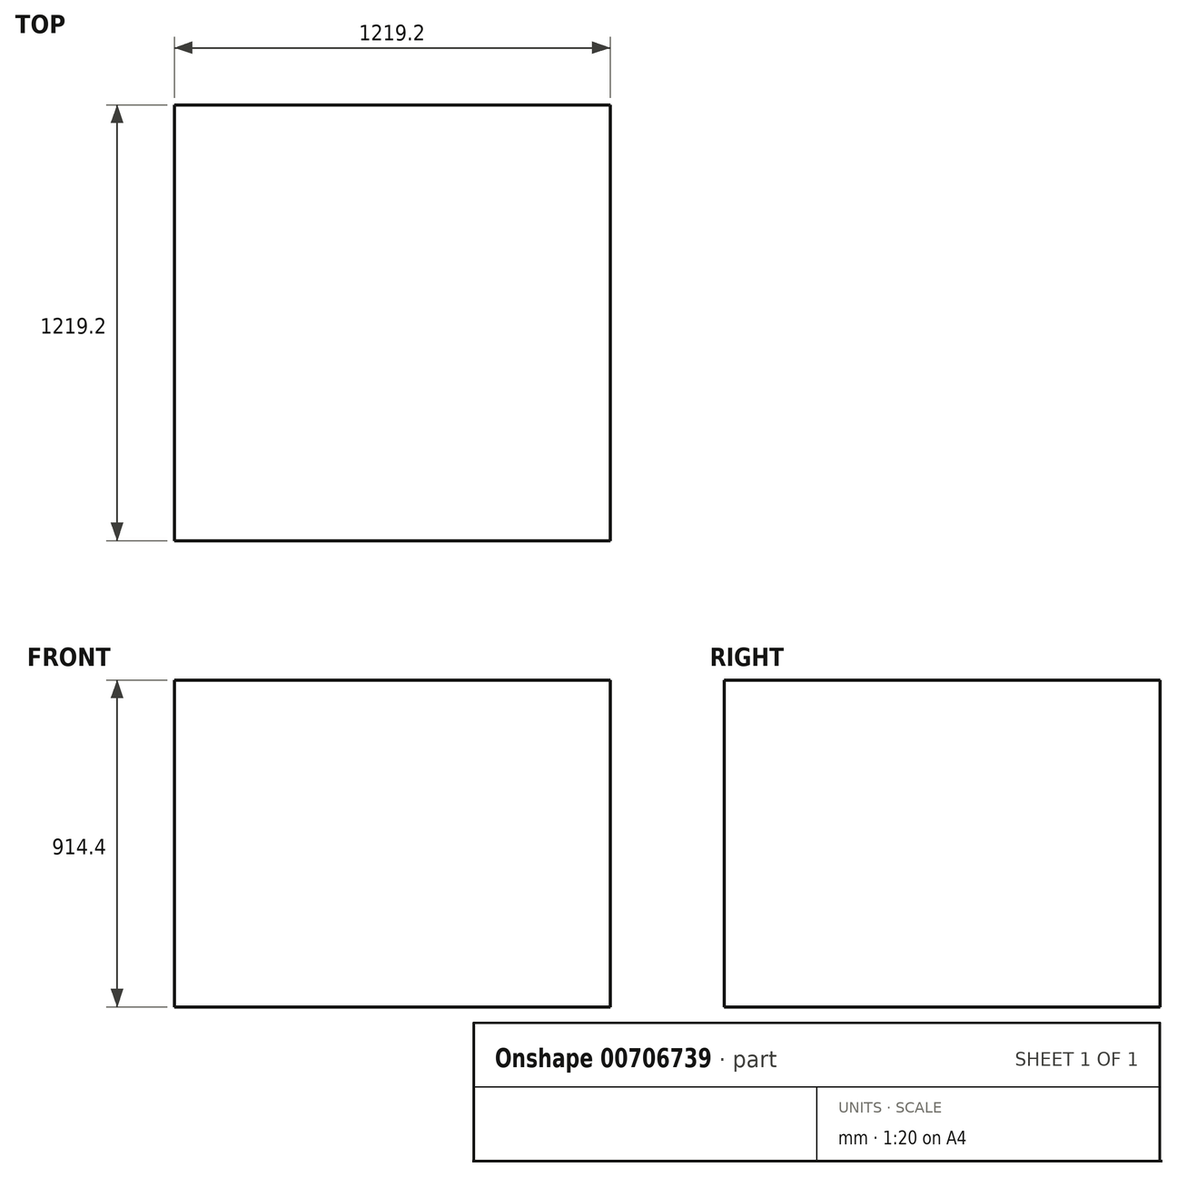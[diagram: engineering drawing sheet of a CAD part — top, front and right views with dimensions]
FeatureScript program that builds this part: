
annotation { "Feature Type Name" : "Feature", "Feature Type Description" : "" }
export const myFeature = defineFeature(function(context is Context, id is Id, definition is map)
    precondition{}
    {
        {
            var Q0;
            Q0=qCreatedBy(makeId("Top.planeOp"),FACE);
            var sketch = newSketch(context, id + "F0", { "sketchPlane" : qUnion([Q0])});
            skLineSegment(sketch, "E0.bottom", {"start": v(-76.57, 1143.75) * mm, "end": v(1142.63, 1143.75) * mm});
            skLineSegment(sketch, "E0.top", {"start": v(-76.57, -75.45) * mm, "end": v(1142.63, -75.45) * mm});
            skLineSegment(sketch, "E0.left", {"start": v(-76.57, 1143.75) * mm, "end": v(-76.57, -75.45) * mm});
            skLineSegment(sketch, "E0.right", {"start": v(1142.63, 1143.75) * mm, "end": v(1142.63, -75.45) * mm});
            skSolve(sketch);
        }
        {
            var Q0;
            Q0=makeQuery(id+"F0.imprint","IMPRINT",FACE,{"disambiguationData":[TD([[makeQuery(id+"F0.imprint","IMPRINT",EDGE,{"derivedFrom":sQuery(id+"F0.wireOp",EDGE,"E0.bottom")}),-1.0]])]});
            extrude(context, id + "F1", {"entities" : qUnion([Q0]), "depth" : 914.4 * mm, "offsetDistance" : 25.4 * mm});
        }
    });
